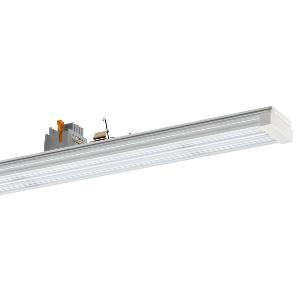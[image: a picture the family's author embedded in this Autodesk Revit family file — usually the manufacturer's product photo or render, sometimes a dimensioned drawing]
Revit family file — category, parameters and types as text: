
# Revit family: conveo_-_cvg_15000_840_w-p_da_7_226848059-00804941_360e
name_source: partatom
category: Lighting Fixtures
units: mm (PartAtom-declared; Revit-internal decimal feet)

## family parameters
Cut with Voids When Loaded = No
Host = Face
Light Source = No
Part Type = Normal
Room Calculation Point = No
Round Connector Dimension = Use Diameter
Shared = No

## types (1)
- CONVEO - CVG 15000/840/W-P/DA/7 (1 x LED, 14700 lm, 4000K)
    Apparent Load = 100 VA
    Approval mark = CE
    CIE Flux Codes = 54 85 97 100 100
    Color Rendering = 80-89
    Color Temperature = 4000K
    Control Gear = Electronic ballast
    Default Elevation = 1800 mm
    Description = CVG 15000/840/W-P/DA/7|Continuous-row system|light source: LED|work equipment: Adjustable electronic ballast, digital DALI|connected load: 220-240 V, 50-60 Hz|Power consumption: approx. 100 W|luminous flux: 14700 lm|luminous efficacy: 147 lm/W|colour temperature: Cold white, ca. 4000 K|color rendering index (CRI): >= 80|chromaticity tolerance:  3 SDCM|System of protection: IP 54|class of protection: I|technology: Continuously dimmable|luminaire body|material: Aluminium|surface: Powder coatet|colour: White|lamp cover: Acrylic (PMMA), Satine|weight (net): approx. 2.2 kg|Fastening: Available separately|minimum ambient temperature: -25 ░C|maximum ambient temperature: 33 ░C|glare control: Prism optics (linear)|Approval mark: VDE - ENEC|
    Frequency = 50 Hz
    Height = 70 mm
    Lamp = 1 x LED
    Lamp Light Flux = 14700 lm
    Lamp count = 1
    Length = 1500 mm
    Luminous efficacy = 147 lm/W
    Manufacturer = Waldmann
    ModVariant = No
    Model = 226848059-00804941
    Mounting Place = Ceiling
    Mounting Type = Pendant
    Number of Poles = 1
    OnlyDefault = Yes
    Power Factor = 1
    Product Name = CONVEO - CVG 15000/840/W-P/DA/7
    Product group = Continuous-row system (industry)
    ProductGroupID = 301
    Protection Class = Protection class I
    Protection Degree = IP 54
    RLX_Detail_Level = 1
    RlxData = <blob elided: 132745 chars, md5=45933a97>
    Socket = socket
    Standby Power = 0 W
    System Light Flux = 14700 lm
    System Power = 100 W
    Type Comments = Product without accessories
    Type Image = 226848059-00804941-2p7.jpg
    URL = http://relux.com
    VarID = ---
    Voltage = 230 V
    Voltage Range = 220-240 V
    Weight = 0.00 kg
    Width = 64 mm

## geometry (parser evidence)
native form markers: Blend x4, Sweep x9
no freeform markers — native parametric forms only
